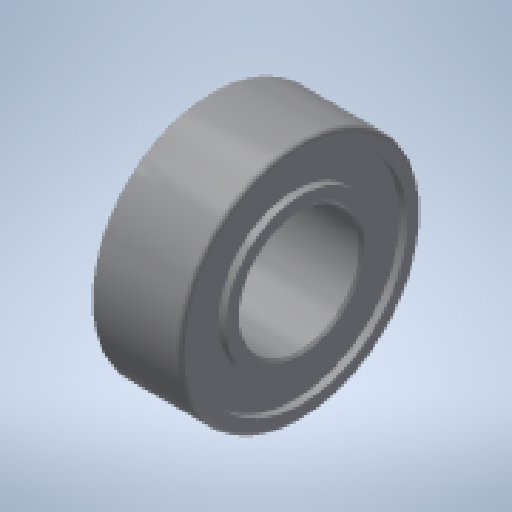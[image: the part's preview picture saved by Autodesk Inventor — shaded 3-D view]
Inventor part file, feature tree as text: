
AUTODESK INVENTOR PART (.ipt)
format: ipt  version: 2023 (Build 270158000, 158)  size: 198,656 bytes
history: native  units: in
note: dims shown in document units (in); Inventor stores cm internally (conversion verified against a paired STEP export)
features: chamfer x1
ambient origin geometry x8: Origin, YZ Plane, XZ Plane, XY Plane, X Axis, Y Axis, Z Axis, Center Point
bodies: Solid1 (feature_tree)
feature tree (1):
  chamfer  "Chamfer1"  [1 undecoded]
note: 1 required parameter value undecoded (feature->parameter linkage not recoverable at this tier; creation-order binding heuristic only, values carry confidence <= 0.55)
